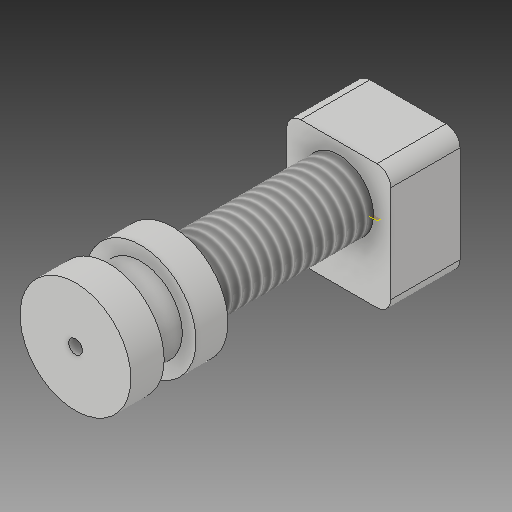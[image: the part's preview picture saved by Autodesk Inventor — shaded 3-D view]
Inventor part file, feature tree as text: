
AUTODESK INVENTOR PART (.ipt)
format: ipt  version: 2018 (Build 220112000, 112)  size: 219,136 bytes
history: native  units: mm
features: sketch x10, extrude x7, projected_geometry x4, other x3, thread x1, plane x1, revolve x1, hole x1, reference x1
ambient origin geometry x8: Origin, YZ Plane, XZ Plane, XY Plane, X Axis, Y Axis, Z Axis, Center Point
bodies: Solid1 (feature_tree)
feature tree (29):
  extrude  "Extrusion1"  Depth=12.0mm
  extrude  "Extrusion2"  Depth=4.6mm TaperAngle=0.0deg
  extrude  "Extrusion3"  Depth=10.0mm TaperAngle=0.0deg
  extrude  "Extrusion4"  Depth=10.0mm
  thread  "Thread1"  [1 undecoded]
  extrude  "Extrusion5"  Depth=10.0mm TaperAngle=0.0deg
  sketch  "Sketch6"  dims[d17=2.3mm d18=-6.622mm]
  plane  "Work Plane1"
  revolve  "Revolution1"  [1 undecoded]
  extrude  "Extrusion6"  TaperAngle=90.0deg  [1 undecoded]
  extrude  "Extrusion7"  Depth=4.75mm TaperAngle=0.0deg
  hole  "Hole1"  [1 undecoded]
  sketch  "Sketch1"  dims[d0=4.8mm d1=0.0mm d2=12.0mm]
  reference  "Reference1"
  sketch  "Sketch2"  dims[d3=4.6mm d4=0.0mm d5=4.6mm d6=0.0mm]
  projected_geometry  "Projected Loop1"
  sketch  "Sketch3"  dims[d7=10.0mm d8=24.0mm d9=0.0mm]
  projected_geometry  "Projected Loop2"
  sketch  "Sketch4"  dims[d10=10.0mm d11=0.0mm d12=15.0mm d13=18.0mm]
  projected_geometry  "Projected Loop3"
  sketch  "Sketch5"  dims[d14=2.0mm d15=10.0mm d16=0.0mm]
  sketch  "Sketch7"  dims[d20=180.0deg d21=90.0deg]
  sketch  "Sketch8"  dims[d22=0.2mm d23=4.75mm d24=0.0mm]
  sketch  "Sketch9"  dims[d25=10.0mm d26=0.0mm]
  sketch  "Sketch10"  dims[d27=2.0mm d28=6.0mm d29=4.0mm d30=2.0mm d31=90.0deg d32=10.0mm d33=20.594885mm]
  projected_geometry  "Projected Loop4"
  other  "<userpath>\OneDrive\Inventor\Beast 3D Printer\Hotend Mount Assembly.iam"
  other  "Hotend Mount Assembly.iam"
  other  "Hotend Clamp P1:1"
note: 4 required parameter values undecoded (feature->parameter linkage not recoverable at this tier; creation-order binding heuristic only, values carry confidence <= 0.55)